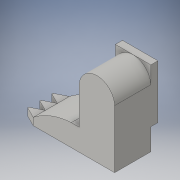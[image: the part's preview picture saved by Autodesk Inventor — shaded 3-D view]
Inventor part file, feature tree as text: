
AUTODESK INVENTOR PART (.ipt)
format: ipt  version: 2016 (Build 200138000, 138)  size: 157,184 bytes
history: native  units: in
note: dims shown in document units (in); Inventor stores cm internally (conversion verified against a paired STEP export)
features: sketch x9, other x3, plane x1
ambient origin geometry x8: Origin, YZ Plane, XZ Plane, XY Plane, X Axis, Y Axis, Z Axis, Center Point
bodies: Solid1 (feature_tree)
feature tree (13):
  other  "Leg.ipt"
  other  "Solid1::Leg.ipt"
  other  "TaggingFeature1"
  sketch  "Sketch1"  dims[d0=0.3937in]
  sketch  "Sketch2"
  sketch  "Sketch3"
  sketch  "Sketch5"
  sketch  "Sketch6"
  sketch  "Sketch7"
  sketch  "Sketch8"
  sketch  "Sketch9"
  sketch  "Sketch10"
  plane  "Work Plane1"
